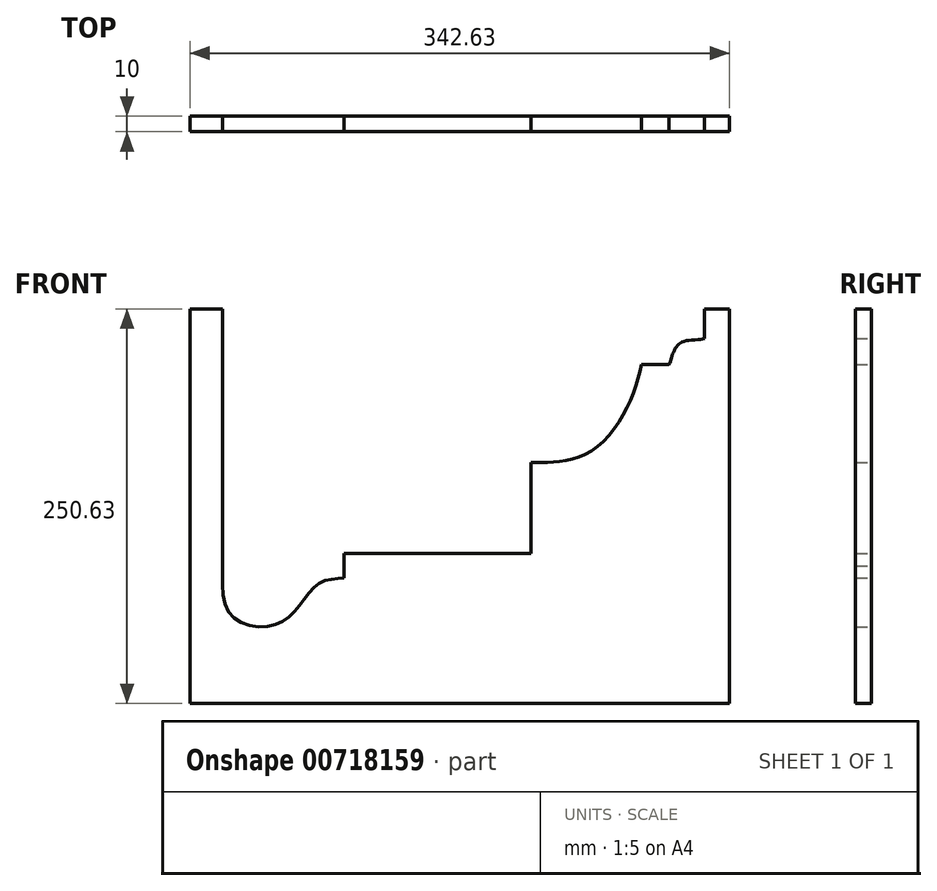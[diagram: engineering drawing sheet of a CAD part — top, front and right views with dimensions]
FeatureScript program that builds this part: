
annotation { "Feature Type Name" : "Feature", "Feature Type Description" : "" }
export const myFeature = defineFeature(function(context is Context, id is Id, definition is map)
    precondition{}
    {
        {
            var Q0;
            Q0=qCreatedBy(makeId("Front.planeOp"),FACE);
            var sketch = newSketch(context, id + "F0", { "sketchPlane" : qUnion([Q0])});
            skLineSegment(sketch, "E0", {"start": v(-91.98, -31.3) * mm, "end": v(-91.98, 131.9) * mm});
            skLineSegment(sketch, "E1", {"start": v(-91.98, 131.9) * mm, "end": v(214.02, 131.9) * mm});
            skLineSegment(sketch, "E2", {"start": v(214.02, 131.9) * mm, "end": v(214.02, 113) * mm});
            skFitSpline(sketch, "E3", {"points": [v(173.96, 96.49) * mm, v(164.3, 68.09) * mm, v(143, 42.11) * mm, v(120.82, 34.97) * mm, v(103.77, 34.25) * mm], "startDerivative": vector(-21.04, -97.25) * mm, "endDerivative": vector(-79.03, -0.85) * mm});
            skLineSegment(sketch, "E4", {"start": v(103.77, 34.25) * mm, "end": v(103.77, -23.3) * mm});
            skLineSegment(sketch, "E5", {"start": v(103.77, -23.3) * mm, "end": v(-14.83, -23.3) * mm});
            skLineSegment(sketch, "E6", {"start": v(-14.83, -23.3) * mm, "end": v(-14.83, -38.85) * mm});
            skLineSegment(sketch, "E7", {"start": v(173.96, 96.49) * mm, "end": v(191.62, 96.49) * mm});
            skFitSpline(sketch, "E8", {"points": [v(191.62, 96.49) * mm, v(193.41, 101.9) * mm, v(196.44, 108.1) * mm, v(202.29, 111.63) * mm, v(214.02, 113) * mm], "startDerivative": vector(12.16, 22.82) * mm, "endDerivative": vector(20.89, 7.04) * mm});
            skFitSpline(sketch, "E9", {"points": [v(-14.83, -38.85) * mm, v(-29.9, -41.88) * mm, v(-43.67, -57.22) * mm, v(-61.41, -69.4) * mm, v(-87.19, -62.12) * mm, v(-91.98, -31.3) * mm], "startDerivative": vector(-86.68, -19.14) * mm, "endDerivative": vector(2.97, 133.5) * mm});
            skSolve(sketch);
        }
        {
            var Q0;
            Q0=makeQuery(id+"F0.imprint","IMPRINT",FACE,{"disambiguationData":[TD([[makeQuery(id+"F0.imprint","IMPRINT",EDGE,{"derivedFrom":sQuery(id+"F0.wireOp",EDGE,"E0")}),-1.0]])]});
            var sketch = newSketch(context, id + "F1", { "sketchPlane" : qUnion([Q0])});
            skPoint(sketch, "E10.0", {"position": v(-91.98, 131.9) * mm});
            skPoint(sketch, "E11.0", {"position": v(214.02, 131.9) * mm});
            skLineSegment(sketch, "E12", {"start": v(-91.98, 131.9) * mm, "end": v(-112.6, 131.9) * mm});
            skLineSegment(sketch, "E13", {"start": v(-112.6, 131.9) * mm, "end": v(-112.6, -118.73) * mm});
            skLineSegment(sketch, "E14", {"start": v(-112.6, -118.73) * mm, "end": v(230.02, -118.73) * mm});
            skLineSegment(sketch, "E15", {"start": v(230.02, -118.73) * mm, "end": v(230.02, 131.9) * mm});
            skLineSegment(sketch, "E16", {"start": v(230.02, 131.9) * mm, "end": v(-91.98, 131.9) * mm});
            skSolve(sketch);
        }
        {
            var Q0;
            Q0=makeQuery(id+"F1.imprint","IMPRINT",FACE,{"disambiguationData":[TD([[makeQuery(id+"F1.imprint","IMPRINT",EDGE,{"derivedFrom":sQuery(id+"F1.wireOp",EDGE,"E12")}),1.0]])]});
            extrude(context, id + "F2", {"entities" : qUnion([Q0]), "depth" : 10 * mm, "offsetDistance" : 25 * mm});
        }
    });
